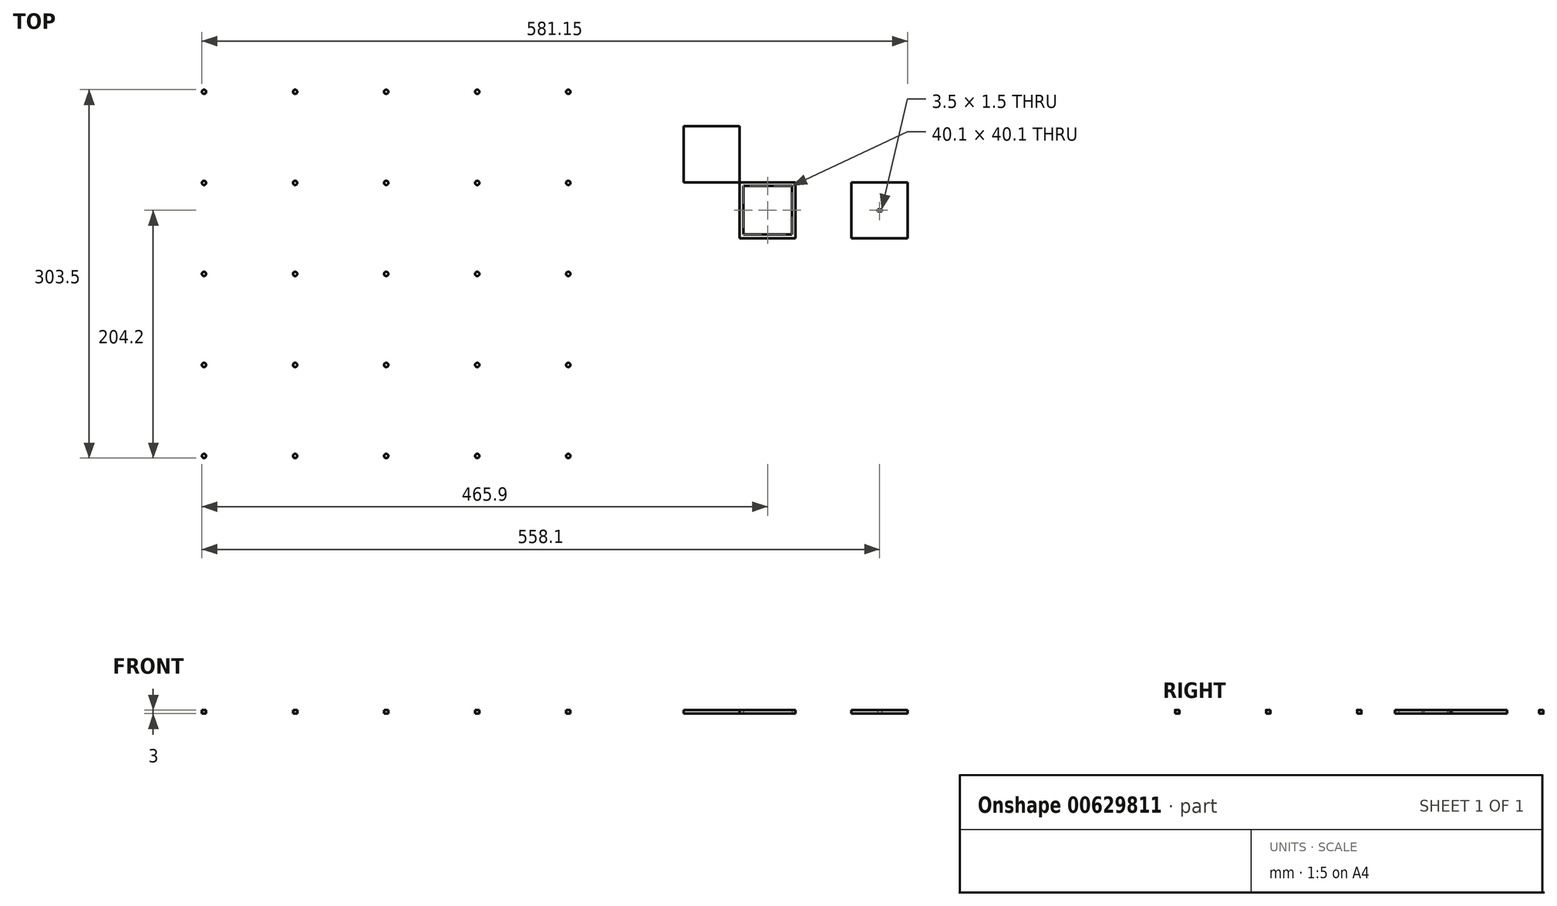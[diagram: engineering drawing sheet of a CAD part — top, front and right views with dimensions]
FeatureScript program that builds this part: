
annotation { "Feature Type Name" : "Feature", "Feature Type Description" : "" }
export const myFeature = defineFeature(function(context is Context, id is Id, definition is map)
    precondition{}
    {
        {
            var Q0;
            Q0=qCreatedBy(makeId("Top.planeOp"),FACE);
            var sketch = newSketch(context, id + "F0", { "sketchPlane" : qUnion([Q0])});
            skLineSegment(sketch, "E0", {"start": v(-292.2, -187.5) * mm, "end": v(-292.2, 187.5) * mm});
            skLineSegment(sketch, "E1", {"start": v(-292.2, 187.5) * mm, "end": v(82.8, 187.5) * mm});
            skLineSegment(sketch, "E2", {"start": v(-292.2, -187.5) * mm, "end": v(82.8, -187.5) * mm});
            skLineSegment(sketch, "E3", {"start": v(-292.2, -112.5) * mm, "end": v(82.8, -112.5) * mm});
            skLineSegment(sketch, "E4", {"start": v(-292.2, -37.5) * mm, "end": v(82.8, -37.5) * mm});
            skLineSegment(sketch, "E5", {"start": v(-292.2, 37.5) * mm, "end": v(82.8, 37.5) * mm});
            skLineSegment(sketch, "E6", {"start": v(-292.2, 112.5) * mm, "end": v(82.8, 112.5) * mm});
            skLineSegment(sketch, "E7", {"start": v(-217.2, -187.5) * mm, "end": v(-217.2, 187.5) * mm});
            skLineSegment(sketch, "E8", {"start": v(-142.2, -187.5) * mm, "end": v(-142.2, 187.5) * mm});
            skLineSegment(sketch, "E9", {"start": v(-67.2, -187.5) * mm, "end": v(-67.2, 187.5) * mm});
            skLineSegment(sketch, "E10", {"start": v(7.8, -187.5) * mm, "end": v(7.8, 187.5) * mm});
            skLineSegment(sketch, "E11", {"start": v(82.8, -187.5) * mm, "end": v(82.8, 187.5) * mm});
            skCircle(sketch, "E12", {"center": v(-212.2, 42.5) * mm, "radius": 1.75 * mm});
            skCircle(sketch, "E13", {"center": v(-62.2, 42.5) * mm, "radius": 1.75 * mm});
            skCircle(sketch, "E14", {"center": v(-137.2, 42.5) * mm, "radius": 1.75 * mm});
            skCircle(sketch, "E15", {"center": v(12.8, 42.5) * mm, "radius": 1.75 * mm});
            skCircle(sketch, "E16", {"center": v(-287.2, 42.5) * mm, "radius": 1.75 * mm});
            skCircle(sketch, "E17", {"center": v(-212.2, 117.5) * mm, "radius": 1.75 * mm});
            skCircle(sketch, "E18", {"center": v(-62.2, 117.5) * mm, "radius": 1.75 * mm});
            skCircle(sketch, "E19", {"center": v(-137.2, 117.5) * mm, "radius": 1.75 * mm});
            skCircle(sketch, "E20", {"center": v(12.8, 117.5) * mm, "radius": 1.75 * mm});
            skCircle(sketch, "E21", {"center": v(-287.2, 117.5) * mm, "radius": 1.75 * mm});
            skCircle(sketch, "E22", {"center": v(-212.2, -182.5) * mm, "radius": 1.75 * mm});
            skCircle(sketch, "E23", {"center": v(-62.2, -182.5) * mm, "radius": 1.75 * mm});
            skCircle(sketch, "E24", {"center": v(-137.2, -182.5) * mm, "radius": 1.75 * mm});
            skCircle(sketch, "E25", {"center": v(-287.2, -182.5) * mm, "radius": 1.75 * mm});
            skCircle(sketch, "E26", {"center": v(-212.2, -32.5) * mm, "radius": 1.75 * mm});
            skCircle(sketch, "E27", {"center": v(-62.2, -32.5) * mm, "radius": 1.75 * mm});
            skCircle(sketch, "E28", {"center": v(-137.2, -32.5) * mm, "radius": 1.75 * mm});
            skCircle(sketch, "E29", {"center": v(12.8, -32.5) * mm, "radius": 1.75 * mm});
            skCircle(sketch, "E30", {"center": v(-287.2, -32.5) * mm, "radius": 1.75 * mm});
            skCircle(sketch, "E31", {"center": v(-137.2, -107.5) * mm, "radius": 1.75 * mm});
            skCircle(sketch, "E32", {"center": v(12.8, -107.5) * mm, "radius": 1.75 * mm});
            skCircle(sketch, "E33", {"center": v(-287.2, -107.5) * mm, "radius": 1.75 * mm});
            skCircle(sketch, "E34", {"center": v(12.8, -182.5) * mm, "radius": 1.75 * mm});
            skCircle(sketch, "E35", {"center": v(-212.2, -107.5) * mm, "radius": 1.75 * mm});
            skCircle(sketch, "E36", {"center": v(-62.2, -107.5) * mm, "radius": 1.75 * mm});
            skCircle(sketch, "E37", {"center": v(-287.2, 107.5) * mm, "radius": 1.75 * mm});
            skCircle(sketch, "E38", {"center": v(-212.2, 107.5) * mm, "radius": 1.75 * mm});
            skCircle(sketch, "E39", {"center": v(-62.2, 107.5) * mm, "radius": 1.75 * mm});
            skCircle(sketch, "E40", {"center": v(-137.2, 107.5) * mm, "radius": 1.75 * mm});
            skCircle(sketch, "E41", {"center": v(12.8, 107.5) * mm, "radius": 1.75 * mm});
            skCircle(sketch, "E42", {"center": v(-287.2, 32.5) * mm, "radius": 1.75 * mm});
            skCircle(sketch, "E43", {"center": v(-212.2, 32.5) * mm, "radius": 1.75 * mm});
            skCircle(sketch, "E44", {"center": v(-62.2, 32.5) * mm, "radius": 1.75 * mm});
            skCircle(sketch, "E45", {"center": v(-137.2, 182.5) * mm, "radius": 1.75 * mm});
            skCircle(sketch, "E46", {"center": v(12.8, 182.5) * mm, "radius": 1.75 * mm});
            skCircle(sketch, "E47", {"center": v(-287.2, 182.5) * mm, "radius": 1.75 * mm});
            skCircle(sketch, "E48", {"center": v(-212.2, 182.5) * mm, "radius": 1.75 * mm});
            skCircle(sketch, "E49", {"center": v(-62.2, 182.5) * mm, "radius": 1.75 * mm});
            skCircle(sketch, "E50", {"center": v(-212.2, -117.5) * mm, "radius": 1.75 * mm});
            skCircle(sketch, "E51", {"center": v(-62.2, -117.5) * mm, "radius": 1.75 * mm});
            skCircle(sketch, "E52", {"center": v(-137.2, -117.5) * mm, "radius": 1.75 * mm});
            skCircle(sketch, "E53", {"center": v(-287.2, -117.5) * mm, "radius": 1.75 * mm});
            skCircle(sketch, "E54", {"center": v(-137.2, 32.5) * mm, "radius": 1.75 * mm});
            skCircle(sketch, "E55", {"center": v(12.8, 32.5) * mm, "radius": 1.75 * mm});
            skCircle(sketch, "E56", {"center": v(12.8, -117.5) * mm, "radius": 1.75 * mm});
            skCircle(sketch, "E57", {"center": v(-287.2, -42.5) * mm, "radius": 1.75 * mm});
            skCircle(sketch, "E58", {"center": v(-212.2, -42.5) * mm, "radius": 1.75 * mm});
            skCircle(sketch, "E59", {"center": v(-62.2, -42.5) * mm, "radius": 1.75 * mm});
            skCircle(sketch, "E60", {"center": v(-137.2, -42.5) * mm, "radius": 1.75 * mm});
            skCircle(sketch, "E61", {"center": v(12.8, -42.5) * mm, "radius": 1.75 * mm});
            skCircle(sketch, "E62", {"center": v(-72.2, 107.5) * mm, "radius": 1.75 * mm});
            skCircle(sketch, "E63", {"center": v(77.8, 107.5) * mm, "radius": 1.75 * mm});
            skCircle(sketch, "E64", {"center": v(-222.2, 107.5) * mm, "radius": 1.75 * mm});
            skCircle(sketch, "E65", {"center": v(-147.2, 107.5) * mm, "radius": 1.75 * mm});
            skCircle(sketch, "E66", {"center": v(2.8, 107.5) * mm, "radius": 1.75 * mm});
            skCircle(sketch, "E67", {"center": v(77.8, 32.5) * mm, "radius": 1.75 * mm});
            skCircle(sketch, "E68", {"center": v(-222.2, 32.5) * mm, "radius": 1.75 * mm});
            skCircle(sketch, "E69", {"center": v(-147.2, 32.5) * mm, "radius": 1.75 * mm});
            skCircle(sketch, "E70", {"center": v(2.8, 32.5) * mm, "radius": 1.75 * mm});
            skCircle(sketch, "E71", {"center": v(-72.2, 32.5) * mm, "radius": 1.75 * mm});
            skCircle(sketch, "E72", {"center": v(77.8, 182.5) * mm, "radius": 1.75 * mm});
            skCircle(sketch, "E73", {"center": v(-222.2, 182.5) * mm, "radius": 1.75 * mm});
            skCircle(sketch, "E74", {"center": v(-147.2, 182.5) * mm, "radius": 1.75 * mm});
            skCircle(sketch, "E75", {"center": v(2.8, 182.5) * mm, "radius": 1.75 * mm});
            skCircle(sketch, "E76", {"center": v(-72.2, 182.5) * mm, "radius": 1.75 * mm});
            skCircle(sketch, "E77", {"center": v(-147.2, -117.5) * mm, "radius": 1.75 * mm});
            skCircle(sketch, "E78", {"center": v(2.8, -117.5) * mm, "radius": 1.75 * mm});
            skCircle(sketch, "E79", {"center": v(-72.2, -117.5) * mm, "radius": 1.75 * mm});
            skCircle(sketch, "E80", {"center": v(-222.2, -117.5) * mm, "radius": 1.75 * mm});
            skCircle(sketch, "E81", {"center": v(77.8, -42.5) * mm, "radius": 1.75 * mm});
            skCircle(sketch, "E82", {"center": v(-222.2, -42.5) * mm, "radius": 1.75 * mm});
            skCircle(sketch, "E83", {"center": v(-147.2, -42.5) * mm, "radius": 1.75 * mm});
            skCircle(sketch, "E84", {"center": v(2.8, -42.5) * mm, "radius": 1.75 * mm});
            skCircle(sketch, "E85", {"center": v(77.8, -117.5) * mm, "radius": 1.75 * mm});
            skCircle(sketch, "E86", {"center": v(-72.2, -42.5) * mm, "radius": 1.75 * mm});
            skLineSegment(sketch, "E87", {"start": v(1.05, 40.75) * mm, "end": v(4.55, 40.75) * mm});
            skLineSegment(sketch, "E88", {"start": v(4.55, 40.75) * mm, "end": v(4.55, 44.25) * mm});
            skLineSegment(sketch, "E89", {"start": v(4.55, 44.25) * mm, "end": v(1.05, 44.25) * mm});
            skLineSegment(sketch, "E90", {"start": v(1.05, 44.25) * mm, "end": v(1.05, 40.75) * mm});
            skLineSegment(sketch, "E91", {"start": v(-223.95, 40.75) * mm, "end": v(-220.45, 40.75) * mm});
            skLineSegment(sketch, "E92", {"start": v(-220.45, 40.75) * mm, "end": v(-220.45, 44.25) * mm});
            skLineSegment(sketch, "E93", {"start": v(-220.45, 44.25) * mm, "end": v(-223.95, 44.25) * mm});
            skLineSegment(sketch, "E94", {"start": v(-223.95, 44.25) * mm, "end": v(-223.95, 40.75) * mm});
            skLineSegment(sketch, "E95", {"start": v(-73.95, 40.75) * mm, "end": v(-70.45, 40.75) * mm});
            skLineSegment(sketch, "E96", {"start": v(-70.45, 40.75) * mm, "end": v(-70.45, 44.25) * mm});
            skLineSegment(sketch, "E97", {"start": v(-70.45, 44.25) * mm, "end": v(-73.95, 44.25) * mm});
            skLineSegment(sketch, "E98", {"start": v(-73.95, 44.25) * mm, "end": v(-73.95, 40.75) * mm});
            skLineSegment(sketch, "E99", {"start": v(76.05, 40.75) * mm, "end": v(79.55, 40.75) * mm});
            skLineSegment(sketch, "E100", {"start": v(79.55, 40.75) * mm, "end": v(79.55, 44.25) * mm});
            skLineSegment(sketch, "E101", {"start": v(79.55, 44.25) * mm, "end": v(76.05, 44.25) * mm});
            skLineSegment(sketch, "E102", {"start": v(76.05, 44.25) * mm, "end": v(76.05, 40.75) * mm});
            skLineSegment(sketch, "E103", {"start": v(-148.95, -34.25) * mm, "end": v(-145.45, -34.25) * mm});
            skLineSegment(sketch, "E104", {"start": v(-145.45, -34.25) * mm, "end": v(-145.45, -30.75) * mm});
            skLineSegment(sketch, "E105", {"start": v(-145.45, -30.75) * mm, "end": v(-148.95, -30.75) * mm});
            skLineSegment(sketch, "E106", {"start": v(-148.95, -30.75) * mm, "end": v(-148.95, -34.25) * mm});
            skLineSegment(sketch, "E107", {"start": v(1.05, -34.25) * mm, "end": v(4.55, -34.25) * mm});
            skLineSegment(sketch, "E108", {"start": v(4.55, -34.25) * mm, "end": v(4.55, -30.75) * mm});
            skLineSegment(sketch, "E109", {"start": v(4.55, -30.75) * mm, "end": v(1.05, -30.75) * mm});
            skLineSegment(sketch, "E110", {"start": v(1.05, -30.75) * mm, "end": v(1.05, -34.25) * mm});
            skLineSegment(sketch, "E111", {"start": v(-223.95, -34.25) * mm, "end": v(-220.45, -34.25) * mm});
            skLineSegment(sketch, "E112", {"start": v(-220.45, -34.25) * mm, "end": v(-220.45, -30.75) * mm});
            skLineSegment(sketch, "E113", {"start": v(-220.45, -30.75) * mm, "end": v(-223.95, -30.75) * mm});
            skLineSegment(sketch, "E114", {"start": v(-223.95, -30.75) * mm, "end": v(-223.95, -34.25) * mm});
            skLineSegment(sketch, "E115", {"start": v(-73.95, -34.25) * mm, "end": v(-70.45, -34.25) * mm});
            skLineSegment(sketch, "E116", {"start": v(-70.45, -34.25) * mm, "end": v(-70.45, -30.75) * mm});
            skLineSegment(sketch, "E117", {"start": v(-70.45, -30.75) * mm, "end": v(-73.95, -30.75) * mm});
            skLineSegment(sketch, "E118", {"start": v(-73.95, -30.75) * mm, "end": v(-73.95, -34.25) * mm});
            skLineSegment(sketch, "E119", {"start": v(76.05, -34.25) * mm, "end": v(79.55, -34.25) * mm});
            skLineSegment(sketch, "E120", {"start": v(79.55, -34.25) * mm, "end": v(79.55, -30.75) * mm});
            skLineSegment(sketch, "E121", {"start": v(79.55, -30.75) * mm, "end": v(76.05, -30.75) * mm});
            skLineSegment(sketch, "E122", {"start": v(76.05, -30.75) * mm, "end": v(76.05, -34.25) * mm});
            skLineSegment(sketch, "E123", {"start": v(-148.95, 115.75) * mm, "end": v(-145.45, 115.75) * mm});
            skLineSegment(sketch, "E124", {"start": v(-145.45, 115.75) * mm, "end": v(-145.45, 119.25) * mm});
            skLineSegment(sketch, "E125", {"start": v(-145.45, 119.25) * mm, "end": v(-148.95, 119.25) * mm});
            skLineSegment(sketch, "E126", {"start": v(-148.95, 119.25) * mm, "end": v(-148.95, 115.75) * mm});
            skLineSegment(sketch, "E127", {"start": v(1.05, 115.75) * mm, "end": v(4.55, 115.75) * mm});
            skLineSegment(sketch, "E128", {"start": v(4.55, 115.75) * mm, "end": v(4.55, 119.25) * mm});
            skLineSegment(sketch, "E129", {"start": v(4.55, 119.25) * mm, "end": v(1.05, 119.25) * mm});
            skLineSegment(sketch, "E130", {"start": v(1.05, 119.25) * mm, "end": v(1.05, 115.75) * mm});
            skLineSegment(sketch, "E131", {"start": v(-223.95, 115.75) * mm, "end": v(-220.45, 115.75) * mm});
            skLineSegment(sketch, "E132", {"start": v(-220.45, 115.75) * mm, "end": v(-220.45, 119.25) * mm});
            skLineSegment(sketch, "E133", {"start": v(-220.45, 119.25) * mm, "end": v(-223.95, 119.25) * mm});
            skLineSegment(sketch, "E134", {"start": v(-223.95, 119.25) * mm, "end": v(-223.95, 115.75) * mm});
            skLineSegment(sketch, "E135", {"start": v(-73.95, 115.75) * mm, "end": v(-70.45, 115.75) * mm});
            skLineSegment(sketch, "E136", {"start": v(-70.45, 115.75) * mm, "end": v(-70.45, 119.25) * mm});
            skLineSegment(sketch, "E137", {"start": v(-70.45, 119.25) * mm, "end": v(-73.95, 119.25) * mm});
            skLineSegment(sketch, "E138", {"start": v(-73.95, 119.25) * mm, "end": v(-73.95, 115.75) * mm});
            skLineSegment(sketch, "E139", {"start": v(76.05, 115.75) * mm, "end": v(79.55, 115.75) * mm});
            skLineSegment(sketch, "E140", {"start": v(79.55, 115.75) * mm, "end": v(79.55, 119.25) * mm});
            skLineSegment(sketch, "E141", {"start": v(79.55, 119.25) * mm, "end": v(76.05, 119.25) * mm});
            skLineSegment(sketch, "E142", {"start": v(76.05, 119.25) * mm, "end": v(76.05, 115.75) * mm});
            skLineSegment(sketch, "E143", {"start": v(-148.95, 40.75) * mm, "end": v(-145.45, 40.75) * mm});
            skLineSegment(sketch, "E144", {"start": v(-145.45, 40.75) * mm, "end": v(-145.45, 44.25) * mm});
            skLineSegment(sketch, "E145", {"start": v(-145.45, 44.25) * mm, "end": v(-148.95, 44.25) * mm});
            skLineSegment(sketch, "E146", {"start": v(-148.95, 44.25) * mm, "end": v(-148.95, 40.75) * mm});
            skLineSegment(sketch, "E147", {"start": v(-223.95, -184.25) * mm, "end": v(-220.45, -184.25) * mm});
            skLineSegment(sketch, "E148", {"start": v(-220.45, -184.25) * mm, "end": v(-220.45, -180.75) * mm});
            skLineSegment(sketch, "E149", {"start": v(-220.45, -180.75) * mm, "end": v(-223.95, -180.75) * mm});
            skLineSegment(sketch, "E150", {"start": v(-223.95, -180.75) * mm, "end": v(-223.95, -184.25) * mm});
            skLineSegment(sketch, "E151", {"start": v(-73.95, -184.25) * mm, "end": v(-70.45, -184.25) * mm});
            skLineSegment(sketch, "E152", {"start": v(-70.45, -184.25) * mm, "end": v(-70.45, -180.75) * mm});
            skLineSegment(sketch, "E153", {"start": v(-70.45, -180.75) * mm, "end": v(-73.95, -180.75) * mm});
            skLineSegment(sketch, "E154", {"start": v(-73.95, -180.75) * mm, "end": v(-73.95, -184.25) * mm});
            skLineSegment(sketch, "E155", {"start": v(-148.95, -184.25) * mm, "end": v(-145.45, -184.25) * mm});
            skLineSegment(sketch, "E156", {"start": v(-145.45, -184.25) * mm, "end": v(-145.45, -180.75) * mm});
            skLineSegment(sketch, "E157", {"start": v(-145.45, -180.75) * mm, "end": v(-148.95, -180.75) * mm});
            skLineSegment(sketch, "E158", {"start": v(-148.95, -180.75) * mm, "end": v(-148.95, -184.25) * mm});
            skLineSegment(sketch, "E159", {"start": v(1.05, -109.25) * mm, "end": v(4.55, -109.25) * mm});
            skLineSegment(sketch, "E160", {"start": v(4.55, -109.25) * mm, "end": v(4.55, -105.75) * mm});
            skLineSegment(sketch, "E161", {"start": v(4.55, -105.75) * mm, "end": v(1.05, -105.75) * mm});
            skLineSegment(sketch, "E162", {"start": v(1.05, -105.75) * mm, "end": v(1.05, -109.25) * mm});
            skLineSegment(sketch, "E163", {"start": v(-223.95, -109.25) * mm, "end": v(-220.45, -109.25) * mm});
            skLineSegment(sketch, "E164", {"start": v(-220.45, -109.25) * mm, "end": v(-220.45, -105.75) * mm});
            skLineSegment(sketch, "E165", {"start": v(-220.45, -105.75) * mm, "end": v(-223.95, -105.75) * mm});
            skLineSegment(sketch, "E166", {"start": v(-223.95, -105.75) * mm, "end": v(-223.95, -109.25) * mm});
            skLineSegment(sketch, "E167", {"start": v(-73.95, -109.25) * mm, "end": v(-70.45, -109.25) * mm});
            skLineSegment(sketch, "E168", {"start": v(-70.45, -109.25) * mm, "end": v(-70.45, -105.75) * mm});
            skLineSegment(sketch, "E169", {"start": v(-70.45, -105.75) * mm, "end": v(-73.95, -105.75) * mm});
            skLineSegment(sketch, "E170", {"start": v(-73.95, -105.75) * mm, "end": v(-73.95, -109.25) * mm});
            skLineSegment(sketch, "E171", {"start": v(76.05, -109.25) * mm, "end": v(79.55, -109.25) * mm});
            skLineSegment(sketch, "E172", {"start": v(79.55, -109.25) * mm, "end": v(79.55, -105.75) * mm});
            skLineSegment(sketch, "E173", {"start": v(79.55, -105.75) * mm, "end": v(76.05, -105.75) * mm});
            skLineSegment(sketch, "E174", {"start": v(76.05, -105.75) * mm, "end": v(76.05, -109.25) * mm});
            skLineSegment(sketch, "E175", {"start": v(-148.95, -109.25) * mm, "end": v(-145.45, -109.25) * mm});
            skLineSegment(sketch, "E176", {"start": v(-145.45, -109.25) * mm, "end": v(-145.45, -105.75) * mm});
            skLineSegment(sketch, "E177", {"start": v(-145.45, -105.75) * mm, "end": v(-148.95, -105.75) * mm});
            skLineSegment(sketch, "E178", {"start": v(-148.95, -105.75) * mm, "end": v(-148.95, -109.25) * mm});
            skLineSegment(sketch, "E179", {"start": v(76.05, -184.25) * mm, "end": v(79.55, -184.25) * mm});
            skLineSegment(sketch, "E180", {"start": v(79.55, -184.25) * mm, "end": v(79.55, -180.75) * mm});
            skLineSegment(sketch, "E181", {"start": v(79.55, -180.75) * mm, "end": v(76.05, -180.75) * mm});
            skLineSegment(sketch, "E182", {"start": v(76.05, -180.75) * mm, "end": v(76.05, -184.25) * mm});
            skLineSegment(sketch, "E183", {"start": v(1.05, -184.25) * mm, "end": v(4.55, -184.25) * mm});
            skLineSegment(sketch, "E184", {"start": v(4.55, -184.25) * mm, "end": v(4.55, -180.75) * mm});
            skLineSegment(sketch, "E185", {"start": v(4.55, -180.75) * mm, "end": v(1.05, -180.75) * mm});
            skLineSegment(sketch, "E186", {"start": v(1.05, -180.75) * mm, "end": v(1.05, -184.25) * mm});
            skLineSegment(sketch, "E187", {"start": v(-127.7, 127) * mm, "end": v(-81.7, 127) * mm});
            skLineSegment(sketch, "E188", {"start": v(-81.7, 127) * mm, "end": v(-81.7, 173) * mm});
            skLineSegment(sketch, "E189", {"start": v(-81.7, 173) * mm, "end": v(-127.7, 173) * mm});
            skLineSegment(sketch, "E190", {"start": v(-127.7, 173) * mm, "end": v(-127.7, 127) * mm});
            skLineSegment(sketch, "E191", {"start": v(-127.7, -173) * mm, "end": v(-81.7, -173) * mm});
            skLineSegment(sketch, "E192", {"start": v(-81.7, -173) * mm, "end": v(-81.7, -127) * mm});
            skLineSegment(sketch, "E193", {"start": v(-81.7, -127) * mm, "end": v(-127.7, -127) * mm});
            skLineSegment(sketch, "E194", {"start": v(-127.7, -127) * mm, "end": v(-127.7, -173) * mm});
            skLineSegment(sketch, "E195", {"start": v(-50.82, 125.27) * mm, "end": v(-4.97, 128.88) * mm});
            skLineSegment(sketch, "E196", {"start": v(-4.97, 128.88) * mm, "end": v(-8.58, 174.73) * mm});
            skLineSegment(sketch, "E197", {"start": v(-8.58, 174.73) * mm, "end": v(-54.43, 171.12) * mm});
            skLineSegment(sketch, "E198", {"start": v(-54.43, 171.12) * mm, "end": v(-50.82, 125.27) * mm});
            skLineSegment(sketch, "E199", {"start": v(26.18, 123.69) * mm, "end": v(71.61, 130.88) * mm});
            skLineSegment(sketch, "E200", {"start": v(71.61, 130.88) * mm, "end": v(64.42, 176.31) * mm});
            skLineSegment(sketch, "E201", {"start": v(64.42, 176.31) * mm, "end": v(18.99, 169.12) * mm});
            skLineSegment(sketch, "E202", {"start": v(18.99, 169.12) * mm, "end": v(26.18, 123.69) * mm});
            skLineSegment(sketch, "E203", {"start": v(-271.7, 47.27) * mm, "end": v(-226.97, 58) * mm});
            skLineSegment(sketch, "E204", {"start": v(-226.97, 58) * mm, "end": v(-237.7, 102.73) * mm});
            skLineSegment(sketch, "E205", {"start": v(-237.7, 102.73) * mm, "end": v(-282.43, 92) * mm});
            skLineSegment(sketch, "E206", {"start": v(-282.43, 92) * mm, "end": v(-271.7, 47.27) * mm});
            skLineSegment(sketch, "E207", {"start": v(-194.47, 46.02) * mm, "end": v(-150.72, 60.23) * mm});
            skLineSegment(sketch, "E208", {"start": v(-150.72, 60.23) * mm, "end": v(-164.93, 103.98) * mm});
            skLineSegment(sketch, "E209", {"start": v(-164.93, 103.98) * mm, "end": v(-208.68, 89.77) * mm});
            skLineSegment(sketch, "E210", {"start": v(-208.68, 89.77) * mm, "end": v(-194.47, 46.02) * mm});
            skLineSegment(sketch, "E211", {"start": v(-117.15, 44.95) * mm, "end": v(-74.65, 62.55) * mm});
            skLineSegment(sketch, "E212", {"start": v(-74.65, 62.55) * mm, "end": v(-92.25, 105.05) * mm});
            skLineSegment(sketch, "E213", {"start": v(-92.25, 105.05) * mm, "end": v(-134.75, 87.45) * mm});
            skLineSegment(sketch, "E214", {"start": v(-134.75, 87.45) * mm, "end": v(-117.15, 44.95) * mm});
            skLineSegment(sketch, "E215", {"start": v(-39.75, 44.07) * mm, "end": v(1.23, 64.95) * mm});
            skLineSegment(sketch, "E216", {"start": v(1.23, 64.95) * mm, "end": v(-19.65, 105.93) * mm});
            skLineSegment(sketch, "E217", {"start": v(-19.65, 105.93) * mm, "end": v(-60.63, 85.05) * mm});
            skLineSegment(sketch, "E218", {"start": v(-60.63, 85.05) * mm, "end": v(-39.75, 44.07) * mm});
            skLineSegment(sketch, "E219", {"start": v(37.7, 43.37) * mm, "end": v(76.93, 67.4) * mm});
            skLineSegment(sketch, "E220", {"start": v(76.93, 67.4) * mm, "end": v(52.9, 106.63) * mm});
            skLineSegment(sketch, "E221", {"start": v(52.9, 106.63) * mm, "end": v(13.67, 82.6) * mm});
            skLineSegment(sketch, "E222", {"start": v(13.67, 82.6) * mm, "end": v(37.7, 43.37) * mm});
            skLineSegment(sketch, "E223", {"start": v(-259.79, -32.13) * mm, "end": v(-222.57, -5.09) * mm});
            skLineSegment(sketch, "E224", {"start": v(-222.57, -5.09) * mm, "end": v(-249.61, 32.13) * mm});
            skLineSegment(sketch, "E225", {"start": v(-249.61, 32.13) * mm, "end": v(-286.83, 5.09) * mm});
            skLineSegment(sketch, "E226", {"start": v(-286.83, 5.09) * mm, "end": v(-259.79, -32.13) * mm});
            skLineSegment(sketch, "E227", {"start": v(-182.25, -32.43) * mm, "end": v(-147.27, -2.55) * mm});
            skLineSegment(sketch, "E228", {"start": v(-147.27, -2.55) * mm, "end": v(-177.15, 32.43) * mm});
            skLineSegment(sketch, "E229", {"start": v(-177.15, 32.43) * mm, "end": v(-212.13, 2.55) * mm});
            skLineSegment(sketch, "E230", {"start": v(-212.13, 2.55) * mm, "end": v(-182.25, -32.43) * mm});
            skLineSegment(sketch, "E231", {"start": v(-104.7, -32.53) * mm, "end": v(-72.17, 0) * mm});
            skLineSegment(sketch, "E232", {"start": v(-72.17, 0) * mm, "end": v(-104.7, 32.53) * mm});
            skLineSegment(sketch, "E233", {"start": v(-104.7, 32.53) * mm, "end": v(-137.23, 0) * mm});
            skLineSegment(sketch, "E234", {"start": v(-137.23, 0) * mm, "end": v(-104.7, -32.53) * mm});
            skLineSegment(sketch, "E235", {"start": v(-27.15, -32.43) * mm, "end": v(2.73, 2.55) * mm});
            skLineSegment(sketch, "E236", {"start": v(2.73, 2.55) * mm, "end": v(-32.25, 32.43) * mm});
            skLineSegment(sketch, "E237", {"start": v(-32.25, 32.43) * mm, "end": v(-62.13, -2.55) * mm});
            skLineSegment(sketch, "E238", {"start": v(-62.13, -2.55) * mm, "end": v(-27.15, -32.43) * mm});
            skLineSegment(sketch, "E239", {"start": v(50.39, -32.13) * mm, "end": v(77.43, 5.09) * mm});
            skLineSegment(sketch, "E240", {"start": v(77.43, 5.09) * mm, "end": v(40.21, 32.13) * mm});
            skLineSegment(sketch, "E241", {"start": v(40.21, 32.13) * mm, "end": v(13.17, -5.09) * mm});
            skLineSegment(sketch, "E242", {"start": v(13.17, -5.09) * mm, "end": v(50.39, -32.13) * mm});
            skLineSegment(sketch, "E243", {"start": v(-247.1, -106.63) * mm, "end": v(-223.07, -67.4) * mm});
            skLineSegment(sketch, "E244", {"start": v(-223.07, -67.4) * mm, "end": v(-262.3, -43.37) * mm});
            skLineSegment(sketch, "E245", {"start": v(-262.3, -43.37) * mm, "end": v(-286.33, -82.6) * mm});
            skLineSegment(sketch, "E246", {"start": v(-286.33, -82.6) * mm, "end": v(-247.1, -106.63) * mm});
            skLineSegment(sketch, "E247", {"start": v(-169.65, -105.93) * mm, "end": v(-148.77, -64.95) * mm});
            skLineSegment(sketch, "E248", {"start": v(-148.77, -64.95) * mm, "end": v(-189.75, -44.07) * mm});
            skLineSegment(sketch, "E249", {"start": v(-189.75, -44.07) * mm, "end": v(-210.63, -85.05) * mm});
            skLineSegment(sketch, "E250", {"start": v(-210.63, -85.05) * mm, "end": v(-169.65, -105.93) * mm});
            skLineSegment(sketch, "E251", {"start": v(-92.25, -105.05) * mm, "end": v(-74.65, -62.55) * mm});
            skLineSegment(sketch, "E252", {"start": v(-74.65, -62.55) * mm, "end": v(-117.15, -44.95) * mm});
            skLineSegment(sketch, "E253", {"start": v(-117.15, -44.95) * mm, "end": v(-134.75, -87.45) * mm});
            skLineSegment(sketch, "E254", {"start": v(-134.75, -87.45) * mm, "end": v(-92.25, -105.05) * mm});
            skLineSegment(sketch, "E255", {"start": v(-14.93, -103.98) * mm, "end": v(-0.72, -60.23) * mm});
            skLineSegment(sketch, "E256", {"start": v(-0.72, -60.23) * mm, "end": v(-44.47, -46.02) * mm});
            skLineSegment(sketch, "E257", {"start": v(-44.47, -46.02) * mm, "end": v(-58.68, -89.77) * mm});
            skLineSegment(sketch, "E258", {"start": v(-58.68, -89.77) * mm, "end": v(-14.93, -103.98) * mm});
            skLineSegment(sketch, "E259", {"start": v(62.3, -102.73) * mm, "end": v(73.03, -58) * mm});
            skLineSegment(sketch, "E260", {"start": v(73.03, -58) * mm, "end": v(28.3, -47.27) * mm});
            skLineSegment(sketch, "E261", {"start": v(28.3, -47.27) * mm, "end": v(17.57, -92) * mm});
            skLineSegment(sketch, "E262", {"start": v(17.57, -92) * mm, "end": v(62.3, -102.73) * mm});
            skLineSegment(sketch, "E263", {"start": v(-235.58, -176.31) * mm, "end": v(-228.39, -130.88) * mm});
            skLineSegment(sketch, "E264", {"start": v(-228.39, -130.88) * mm, "end": v(-273.82, -123.69) * mm});
            skLineSegment(sketch, "E265", {"start": v(-273.82, -123.69) * mm, "end": v(-281.01, -169.12) * mm});
            skLineSegment(sketch, "E266", {"start": v(-281.01, -169.12) * mm, "end": v(-235.58, -176.31) * mm});
            skLineSegment(sketch, "E267", {"start": v(-158.58, -174.73) * mm, "end": v(-154.97, -128.88) * mm});
            skLineSegment(sketch, "E268", {"start": v(-154.97, -128.88) * mm, "end": v(-200.82, -125.27) * mm});
            skLineSegment(sketch, "E269", {"start": v(-200.82, -125.27) * mm, "end": v(-204.43, -171.12) * mm});
            skLineSegment(sketch, "E270", {"start": v(-204.43, -171.12) * mm, "end": v(-158.58, -174.73) * mm});
            skLineSegment(sketch, "E271", {"start": v(107.8, -187.5) * mm, "end": v(107.8, 89.1) * mm});
            skLineSegment(sketch, "E272", {"start": v(107.8, 43) * mm, "end": v(292.2, 43) * mm});
            skLineSegment(sketch, "E273", {"start": v(107.8, -187.5) * mm, "end": v(292.2, -187.5) * mm});
            skLineSegment(sketch, "E274", {"start": v(153.9, -187.5) * mm, "end": v(153.9, 89.1) * mm});
            skLineSegment(sketch, "E275", {"start": v(200, -187.5) * mm, "end": v(200, 43) * mm});
            skLineSegment(sketch, "E276", {"start": v(246.1, -187.5) * mm, "end": v(246.1, 43) * mm});
            skLineSegment(sketch, "E277", {"start": v(292.2, -187.5) * mm, "end": v(292.2, 43) * mm});
            skLineSegment(sketch, "E278", {"start": v(107.8, -3.1) * mm, "end": v(292.2, -3.1) * mm});
            skLineSegment(sketch, "E279", {"start": v(107.8, -49.2) * mm, "end": v(292.2, -49.2) * mm});
            skLineSegment(sketch, "E280", {"start": v(107.8, -95.3) * mm, "end": v(292.2, -95.3) * mm});
            skLineSegment(sketch, "E281", {"start": v(107.8, -141.4) * mm, "end": v(292.2, -141.4) * mm});
            skLineSegment(sketch, "E282", {"start": v(110.8, -46.2) * mm, "end": v(110.8, -6.1) * mm});
            skLineSegment(sketch, "E283", {"start": v(110.8, -138.4) * mm, "end": v(110.8, -98.3) * mm});
            skLineSegment(sketch, "E284", {"start": v(110.8, -184.5) * mm, "end": v(110.8, -144.4) * mm});
            skLineSegment(sketch, "E285", {"start": v(110.8, -92.3) * mm, "end": v(110.8, -52.2) * mm});
            skLineSegment(sketch, "E286", {"start": v(110.8, -0.1) * mm, "end": v(110.8, 40) * mm});
            skLineSegment(sketch, "E287", {"start": v(150.9, -184.5) * mm, "end": v(150.9, -144.4) * mm});
            skLineSegment(sketch, "E288", {"start": v(150.9, -138.4) * mm, "end": v(150.9, -98.3) * mm});
            skLineSegment(sketch, "E289", {"start": v(150.9, -46.2) * mm, "end": v(150.9, -6.1) * mm});
            skLineSegment(sketch, "E290", {"start": v(150.9, -92.3) * mm, "end": v(150.9, -52.2) * mm});
            skLineSegment(sketch, "E291", {"start": v(150.9, -0.1) * mm, "end": v(150.9, 40) * mm});
            skLineSegment(sketch, "E292", {"start": v(156.9, -138.4) * mm, "end": v(156.9, -98.3) * mm});
            skLineSegment(sketch, "E293", {"start": v(156.9, -46.2) * mm, "end": v(156.9, -6.1) * mm});
            skLineSegment(sketch, "E294", {"start": v(156.9, -92.3) * mm, "end": v(156.9, -52.2) * mm});
            skLineSegment(sketch, "E295", {"start": v(156.9, -0.1) * mm, "end": v(156.9, 40) * mm});
            skLineSegment(sketch, "E296", {"start": v(156.9, -184.5) * mm, "end": v(156.9, -144.4) * mm});
            skLineSegment(sketch, "E297", {"start": v(197, -46.2) * mm, "end": v(197, -6.1) * mm});
            skLineSegment(sketch, "E298", {"start": v(197, -92.3) * mm, "end": v(197, -52.2) * mm});
            skLineSegment(sketch, "E299", {"start": v(197, -0.1) * mm, "end": v(197, 40) * mm});
            skLineSegment(sketch, "E300", {"start": v(197, -138.4) * mm, "end": v(197, -98.3) * mm});
            skLineSegment(sketch, "E301", {"start": v(197, -184.5) * mm, "end": v(197, -144.4) * mm});
            skLineSegment(sketch, "E302", {"start": v(203, -92.3) * mm, "end": v(203, -52.2) * mm});
            skLineSegment(sketch, "E303", {"start": v(203, -46.2) * mm, "end": v(203, -6.1) * mm});
            skLineSegment(sketch, "E304", {"start": v(203, -0.1) * mm, "end": v(203, 40) * mm});
            skLineSegment(sketch, "E305", {"start": v(203, -184.5) * mm, "end": v(203, -144.4) * mm});
            skLineSegment(sketch, "E306", {"start": v(203, -138.4) * mm, "end": v(203, -98.3) * mm});
            skLineSegment(sketch, "E307", {"start": v(243.1, -46.2) * mm, "end": v(243.1, -6.1) * mm});
            skLineSegment(sketch, "E308", {"start": v(243.1, -0.1) * mm, "end": v(243.1, 40) * mm});
            skLineSegment(sketch, "E309", {"start": v(243.1, -138.4) * mm, "end": v(243.1, -98.3) * mm});
            skLineSegment(sketch, "E310", {"start": v(243.1, -184.5) * mm, "end": v(243.1, -144.4) * mm});
            skLineSegment(sketch, "E311", {"start": v(243.1, -92.3) * mm, "end": v(243.1, -52.2) * mm});
            skLineSegment(sketch, "E312", {"start": v(249.1, -138.4) * mm, "end": v(249.1, -98.3) * mm});
            skLineSegment(sketch, "E313", {"start": v(249.1, -184.5) * mm, "end": v(249.1, -144.4) * mm});
            skLineSegment(sketch, "E314", {"start": v(249.1, -46.2) * mm, "end": v(249.1, -6.1) * mm});
            skLineSegment(sketch, "E315", {"start": v(249.1, -92.3) * mm, "end": v(249.1, -52.2) * mm});
            skLineSegment(sketch, "E316", {"start": v(289.2, -92.3) * mm, "end": v(289.2, -52.2) * mm});
            skLineSegment(sketch, "E317", {"start": v(289.2, -46.2) * mm, "end": v(289.2, -6.1) * mm});
            skLineSegment(sketch, "E318", {"start": v(289.2, -184.5) * mm, "end": v(289.2, -144.4) * mm});
            skLineSegment(sketch, "E319", {"start": v(289.2, -138.4) * mm, "end": v(289.2, -98.3) * mm});
            skLineSegment(sketch, "E320", {"start": v(203, -0.1) * mm, "end": v(243.1, -0.1) * mm});
            skLineSegment(sketch, "E321", {"start": v(156.9, -0.1) * mm, "end": v(197, -0.1) * mm});
            skLineSegment(sketch, "E322", {"start": v(110.8, -0.1) * mm, "end": v(150.9, -0.1) * mm});
            skLineSegment(sketch, "E323", {"start": v(156.9, -6.1) * mm, "end": v(197, -6.1) * mm});
            skLineSegment(sketch, "E324", {"start": v(203, -6.1) * mm, "end": v(243.1, -6.1) * mm});
            skLineSegment(sketch, "E325", {"start": v(110.8, -6.1) * mm, "end": v(150.9, -6.1) * mm});
            skLineSegment(sketch, "E326", {"start": v(249.1, -6.1) * mm, "end": v(289.2, -6.1) * mm});
            skLineSegment(sketch, "E327", {"start": v(249.1, -46.2) * mm, "end": v(289.2, -46.2) * mm});
            skLineSegment(sketch, "E328", {"start": v(203, -46.2) * mm, "end": v(243.1, -46.2) * mm});
            skLineSegment(sketch, "E329", {"start": v(110.8, -46.2) * mm, "end": v(150.9, -46.2) * mm});
            skLineSegment(sketch, "E330", {"start": v(156.9, -46.2) * mm, "end": v(197, -46.2) * mm});
            skLineSegment(sketch, "E331", {"start": v(156.9, -52.2) * mm, "end": v(197, -52.2) * mm});
            skLineSegment(sketch, "E332", {"start": v(110.8, -52.2) * mm, "end": v(150.9, -52.2) * mm});
            skLineSegment(sketch, "E333", {"start": v(203, -52.2) * mm, "end": v(243.1, -52.2) * mm});
            skLineSegment(sketch, "E334", {"start": v(249.1, -52.2) * mm, "end": v(289.2, -52.2) * mm});
            skLineSegment(sketch, "E335", {"start": v(203, 40) * mm, "end": v(243.1, 40) * mm});
            skLineSegment(sketch, "E336", {"start": v(156.9, 40) * mm, "end": v(197, 40) * mm});
            skLineSegment(sketch, "E337", {"start": v(110.8, 40) * mm, "end": v(150.9, 40) * mm});
            skLineSegment(sketch, "E338", {"start": v(156.9, -92.3) * mm, "end": v(197, -92.3) * mm});
            skLineSegment(sketch, "E339", {"start": v(110.8, -92.3) * mm, "end": v(150.9, -92.3) * mm});
            skLineSegment(sketch, "E340", {"start": v(249.1, -92.3) * mm, "end": v(289.2, -92.3) * mm});
            skLineSegment(sketch, "E341", {"start": v(203, -92.3) * mm, "end": v(243.1, -92.3) * mm});
            skLineSegment(sketch, "E342", {"start": v(156.9, -98.3) * mm, "end": v(197, -98.3) * mm});
            skLineSegment(sketch, "E343", {"start": v(110.8, -98.3) * mm, "end": v(150.9, -98.3) * mm});
            skLineSegment(sketch, "E344", {"start": v(249.1, -98.3) * mm, "end": v(289.2, -98.3) * mm});
            skLineSegment(sketch, "E345", {"start": v(203, -98.3) * mm, "end": v(243.1, -98.3) * mm});
            skLineSegment(sketch, "E346", {"start": v(110.8, -138.4) * mm, "end": v(150.9, -138.4) * mm});
            skLineSegment(sketch, "E347", {"start": v(249.1, -138.4) * mm, "end": v(289.2, -138.4) * mm});
            skLineSegment(sketch, "E348", {"start": v(156.9, -138.4) * mm, "end": v(197, -138.4) * mm});
            skLineSegment(sketch, "E349", {"start": v(203, -138.4) * mm, "end": v(243.1, -138.4) * mm});
            skLineSegment(sketch, "E350", {"start": v(110.8, -144.4) * mm, "end": v(150.9, -144.4) * mm});
            skLineSegment(sketch, "E351", {"start": v(156.9, -144.4) * mm, "end": v(197, -144.4) * mm});
            skLineSegment(sketch, "E352", {"start": v(203, -144.4) * mm, "end": v(243.1, -144.4) * mm});
            skLineSegment(sketch, "E353", {"start": v(249.1, -144.4) * mm, "end": v(289.2, -144.4) * mm});
            skLineSegment(sketch, "E354", {"start": v(110.8, -184.5) * mm, "end": v(150.9, -184.5) * mm});
            skLineSegment(sketch, "E355", {"start": v(249.1, -184.5) * mm, "end": v(289.2, -184.5) * mm});
            skLineSegment(sketch, "E356", {"start": v(156.9, -184.5) * mm, "end": v(197, -184.5) * mm});
            skLineSegment(sketch, "E357", {"start": v(203, -184.5) * mm, "end": v(243.1, -184.5) * mm});
            skLineSegment(sketch, "E358", {"start": v(267.4, 20.7) * mm, "end": v(270.9, 20.7) * mm});
            skLineSegment(sketch, "E359", {"start": v(267.4, 19.2) * mm, "end": v(270.9, 19.2) * mm});
            skLineSegment(sketch, "E360", {"start": v(270.9, 19.2) * mm, "end": v(270.9, 20.7) * mm});
            skLineSegment(sketch, "E361", {"start": v(267.4, 19.2) * mm, "end": v(267.4, 20.7) * mm});
            skLineSegment(sketch, "E362", {"start": v(-27.95, -150.75) * mm, "end": v(-27.95, -149.25) * mm});
            skLineSegment(sketch, "E363", {"start": v(-31.45, -150.75) * mm, "end": v(-31.45, -149.25) * mm});
            skLineSegment(sketch, "E364", {"start": v(43.55, -149.25) * mm, "end": v(47.05, -149.25) * mm});
            skLineSegment(sketch, "E365", {"start": v(-31.45, -149.25) * mm, "end": v(-27.95, -149.25) * mm});
            skLineSegment(sketch, "E366", {"start": v(43.55, -150.75) * mm, "end": v(47.05, -150.75) * mm});
            skLineSegment(sketch, "E367", {"start": v(-31.45, -150.75) * mm, "end": v(-27.95, -150.75) * mm});
            skLineSegment(sketch, "E368", {"start": v(43.55, -150.75) * mm, "end": v(43.55, -149.25) * mm});
            skLineSegment(sketch, "E369", {"start": v(47.05, -150.75) * mm, "end": v(47.05, -149.25) * mm});
            skLineSegment(sketch, "E370", {"start": v(107.8, 89.1) * mm, "end": v(153.9, 89.1) * mm});
            skSolve(sketch);
        }
        {
            var Q0;
            Q0=makeQuery(id+"F0.imprint","IMPRINT",FACE,{"disambiguationData":[TD([[makeQuery(id+"F0.imprint","IMPRINT",EDGE,{"derivedFrom":sQuery(id+"F0.wireOp",EDGE,"E21")}),1.0]])]});
            var Q1;
            Q1=makeQuery(id+"F0.imprint","IMPRINT",FACE,{"disambiguationData":[TD([[makeQuery(id+"F0.imprint","IMPRINT",EDGE,{"derivedFrom":sQuery(id+"F0.wireOp",EDGE,"E12")}),1.0]])]});
            var Q2;
            Q2=makeQuery(id+"F0.imprint","IMPRINT",FACE,{"disambiguationData":[TD([[makeQuery(id+"F0.imprint","IMPRINT",EDGE,{"derivedFrom":sQuery(id+"F0.wireOp",EDGE,"E19")}),1.0]])]});
            var Q3;
            Q3=makeQuery(id+"F0.imprint","IMPRINT",FACE,{"disambiguationData":[TD([[makeQuery(id+"F0.imprint","IMPRINT",EDGE,{"derivedFrom":sQuery(id+"F0.wireOp",EDGE,"E13")}),1.0]])]});
            var Q4;
            Q4=makeQuery(id+"F0.imprint","IMPRINT",FACE,{"disambiguationData":[TD([[makeQuery(id+"F0.imprint","IMPRINT",EDGE,{"derivedFrom":sQuery(id+"F0.wireOp",EDGE,"E20")}),1.0]])]});
            var Q5;
            Q5=makeQuery(id+"F0.imprint","IMPRINT",FACE,{"disambiguationData":[TD([[makeQuery(id+"F0.imprint","IMPRINT",EDGE,{"derivedFrom":sQuery(id+"F0.wireOp",EDGE,"E30")}),1.0]])]});
            var Q6;
            Q6=makeQuery(id+"F0.imprint","IMPRINT",FACE,{"disambiguationData":[TD([[makeQuery(id+"F0.imprint","IMPRINT",EDGE,{"derivedFrom":sQuery(id+"F0.wireOp",EDGE,"E28")}),1.0]])]});
            var Q7;
            Q7=makeQuery(id+"F0.imprint","IMPRINT",FACE,{"disambiguationData":[TD([[makeQuery(id+"F0.imprint","IMPRINT",EDGE,{"derivedFrom":sQuery(id+"F0.wireOp",EDGE,"E29")}),1.0]])]});
            var Q8;
            Q8=makeQuery(id+"F0.imprint","IMPRINT",FACE,{"disambiguationData":[TD([[makeQuery(id+"F0.imprint","IMPRINT",EDGE,{"derivedFrom":sQuery(id+"F0.wireOp",EDGE,"E35")}),1.0]])]});
            var Q9;
            Q9=makeQuery(id+"F0.imprint","IMPRINT",FACE,{"disambiguationData":[TD([[makeQuery(id+"F0.imprint","IMPRINT",EDGE,{"derivedFrom":sQuery(id+"F0.wireOp",EDGE,"E36")}),1.0]])]});
            var Q10;
            Q10=makeQuery(id+"F0.imprint","IMPRINT",FACE,{"disambiguationData":[TD([[makeQuery(id+"F0.imprint","IMPRINT",EDGE,{"derivedFrom":sQuery(id+"F0.wireOp",EDGE,"E25")}),1.0]])]});
            var Q11;
            Q11=makeQuery(id+"F0.imprint","IMPRINT",FACE,{"disambiguationData":[TD([[makeQuery(id+"F0.imprint","IMPRINT",EDGE,{"derivedFrom":sQuery(id+"F0.wireOp",EDGE,"E24")}),1.0]])]});
            var Q12;
            Q12=makeQuery(id+"F0.imprint","IMPRINT",FACE,{"disambiguationData":[TD([[makeQuery(id+"F0.imprint","IMPRINT",EDGE,{"derivedFrom":sQuery(id+"F0.wireOp",EDGE,"E34")}),1.0]])]});
            var Q13;
            {var subQ0=sQuery(id+"F0.wireOp",EDGE,"E370");Q13=makeQuery(id+"F0.imprint","IMPRINT",FACE,{"disambiguationData":[TD([[makeQuery(id+"F0.imprint","IMPRINT",EDGE,{"derivedFrom":subQ0}),-1.0]])]});}
            var Q14;
            Q14=makeQuery(id+"F0.imprint","IMPRINT",FACE,{"disambiguationData":[TD([[makeQuery(id+"F0.imprint","IMPRINT",EDGE,{"derivedFrom":sQuery(id+"F0.wireOp",EDGE,"E295")}),1.0]])]});
            var Q15;
            Q15=makeQuery(id+"F0.imprint","IMPRINT",FACE,{"disambiguationData":[TD([[makeQuery(id+"F0.imprint","IMPRINT",EDGE,{"derivedFrom":sQuery(id+"F0.wireOp",EDGE,"E358")}),1.0]])]});
            extrude(context, id + "F1", {"entities" : qUnion([Q0, Q1, Q2, Q3, Q4, Q5, Q6, Q7, Q8, Q9, Q10, Q11, Q12, Q13, Q14, Q15]), "depth" : 3 * mm, "offsetDistance" : 25 * mm});
        }
        {
            var Q0;
            Q0=makeQuery(id+"F0.imprint","IMPRINT",FACE,{"disambiguationData":[TD([[makeQuery(id+"F0.imprint","IMPRINT",EDGE,{"derivedFrom":sQuery(id+"F0.wireOp",EDGE,"E17")}),1.0]])]});
            var Q1;
            Q1=makeQuery(id+"F0.imprint","IMPRINT",FACE,{"disambiguationData":[TD([[makeQuery(id+"F0.imprint","IMPRINT",EDGE,{"derivedFrom":sQuery(id+"F0.wireOp",EDGE,"E18")}),1.0]])]});
            var Q2;
            Q2=makeQuery(id+"F0.imprint","IMPRINT",FACE,{"disambiguationData":[TD([[makeQuery(id+"F0.imprint","IMPRINT",EDGE,{"derivedFrom":sQuery(id+"F0.wireOp",EDGE,"E16")}),1.0]])]});
            var Q3;
            Q3=makeQuery(id+"F0.imprint","IMPRINT",FACE,{"disambiguationData":[TD([[makeQuery(id+"F0.imprint","IMPRINT",EDGE,{"derivedFrom":sQuery(id+"F0.wireOp",EDGE,"E14")}),1.0]])]});
            var Q4;
            Q4=makeQuery(id+"F0.imprint","IMPRINT",FACE,{"disambiguationData":[TD([[makeQuery(id+"F0.imprint","IMPRINT",EDGE,{"derivedFrom":sQuery(id+"F0.wireOp",EDGE,"E15")}),1.0]])]});
            var Q5;
            Q5=makeQuery(id+"F0.imprint","IMPRINT",FACE,{"disambiguationData":[TD([[makeQuery(id+"F0.imprint","IMPRINT",EDGE,{"derivedFrom":sQuery(id+"F0.wireOp",EDGE,"E26")}),1.0]])]});
            var Q6;
            Q6=makeQuery(id+"F0.imprint","IMPRINT",FACE,{"disambiguationData":[TD([[makeQuery(id+"F0.imprint","IMPRINT",EDGE,{"derivedFrom":sQuery(id+"F0.wireOp",EDGE,"E27")}),1.0]])]});
            var Q7;
            Q7=makeQuery(id+"F0.imprint","IMPRINT",FACE,{"disambiguationData":[TD([[makeQuery(id+"F0.imprint","IMPRINT",EDGE,{"derivedFrom":sQuery(id+"F0.wireOp",EDGE,"E33")}),1.0]])]});
            var Q8;
            Q8=makeQuery(id+"F0.imprint","IMPRINT",FACE,{"disambiguationData":[TD([[makeQuery(id+"F0.imprint","IMPRINT",EDGE,{"derivedFrom":sQuery(id+"F0.wireOp",EDGE,"E31")}),1.0]])]});
            var Q9;
            Q9=makeQuery(id+"F0.imprint","IMPRINT",FACE,{"disambiguationData":[TD([[makeQuery(id+"F0.imprint","IMPRINT",EDGE,{"derivedFrom":sQuery(id+"F0.wireOp",EDGE,"E32")}),1.0]])]});
            var Q10;
            Q10=makeQuery(id+"F0.imprint","IMPRINT",FACE,{"disambiguationData":[TD([[makeQuery(id+"F0.imprint","IMPRINT",EDGE,{"derivedFrom":sQuery(id+"F0.wireOp",EDGE,"E22")}),1.0]])]});
            var Q11;
            Q11=makeQuery(id+"F0.imprint","IMPRINT",FACE,{"disambiguationData":[TD([[makeQuery(id+"F0.imprint","IMPRINT",EDGE,{"derivedFrom":sQuery(id+"F0.wireOp",EDGE,"E23")}),1.0]])]});
            extrude(context, id + "F2", {"entities" : qUnion([Q0, Q1, Q2, Q3, Q4, Q5, Q6, Q7, Q8, Q9, Q10, Q11]), "depth" : 3 * mm, "offsetDistance" : 25 * mm});
        }
    });
